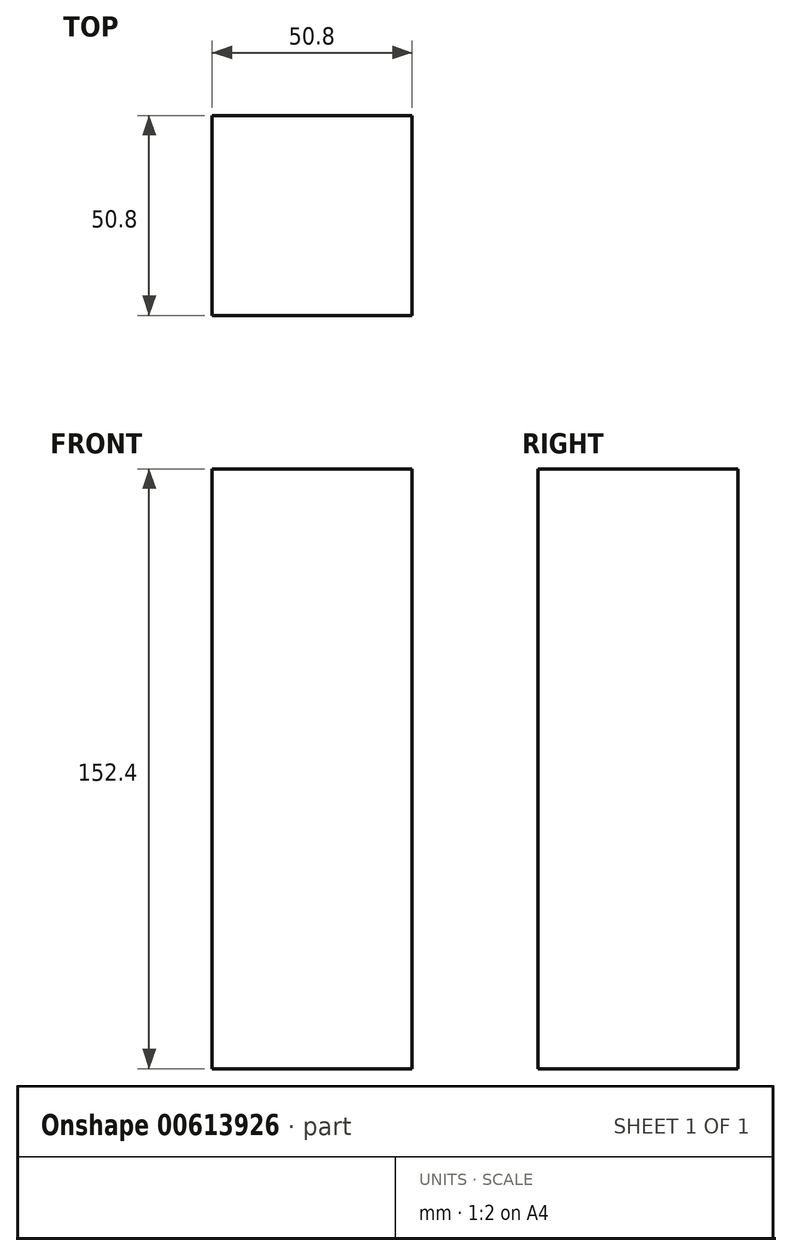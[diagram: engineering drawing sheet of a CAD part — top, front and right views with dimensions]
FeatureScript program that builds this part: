
annotation { "Feature Type Name" : "Feature", "Feature Type Description" : "" }
export const myFeature = defineFeature(function(context is Context, id is Id, definition is map)
    precondition{}
    {
        {
            var Q0;
            Q0=qCreatedBy(makeId("Top.planeOp"),FACE);
            var sketch = newSketch(context, id + "F0", { "sketchPlane" : qUnion([Q0])});
            skLineSegment(sketch, "E0.bottom", {"start": v(-48.42, 29.03) * mm, "end": v(2.38, 29.03) * mm});
            skLineSegment(sketch, "E0.top", {"start": v(-48.42, -21.77) * mm, "end": v(2.38, -21.77) * mm});
            skLineSegment(sketch, "E0.left", {"start": v(-48.42, 29.03) * mm, "end": v(-48.42, -21.77) * mm});
            skLineSegment(sketch, "E0.right", {"start": v(2.38, 29.03) * mm, "end": v(2.38, -21.77) * mm});
            skSolve(sketch);
        }
        {
            var Q0;
            Q0=makeQuery(id+"F0.imprint","IMPRINT",FACE,{"disambiguationData":[TD([[makeQuery(id+"F0.imprint","IMPRINT",EDGE,{"derivedFrom":sQuery(id+"F0.wireOp",EDGE,"E0.bottom")}),-1.0]])]});
            extrude(context, id + "F1", {"entities" : qUnion([Q0]), "depth" : 152.4 * mm, "offsetDistance" : 25.4 * mm});
        }
    });
